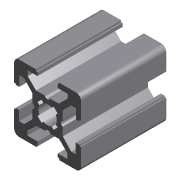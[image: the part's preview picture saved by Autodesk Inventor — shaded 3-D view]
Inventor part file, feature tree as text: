
AUTODESK INVENTOR PART (.ipt)
format: ipt  version: 2011 (Build 150239000, 239)  size: 207,360 bytes
history: native  units: mm (DEFAULTED — no unit token found)
features: extrude x1, sketch x1
ambient origin geometry x8: Origin, YZ Plane, XZ Plane, XY Plane, X Axis, Y Axis, Z Axis, Center Point
bodies: Solid1 (feature_tree)
feature tree (2):
  extrude  "Extrusion1"  [1 undecoded]
  sketch  "Sketch1"  dims[d0=25.4mm d1=0.0mm]
note: 1 required parameter value undecoded (feature->parameter linkage not recoverable at this tier; creation-order binding heuristic only, values carry confidence <= 0.55)
